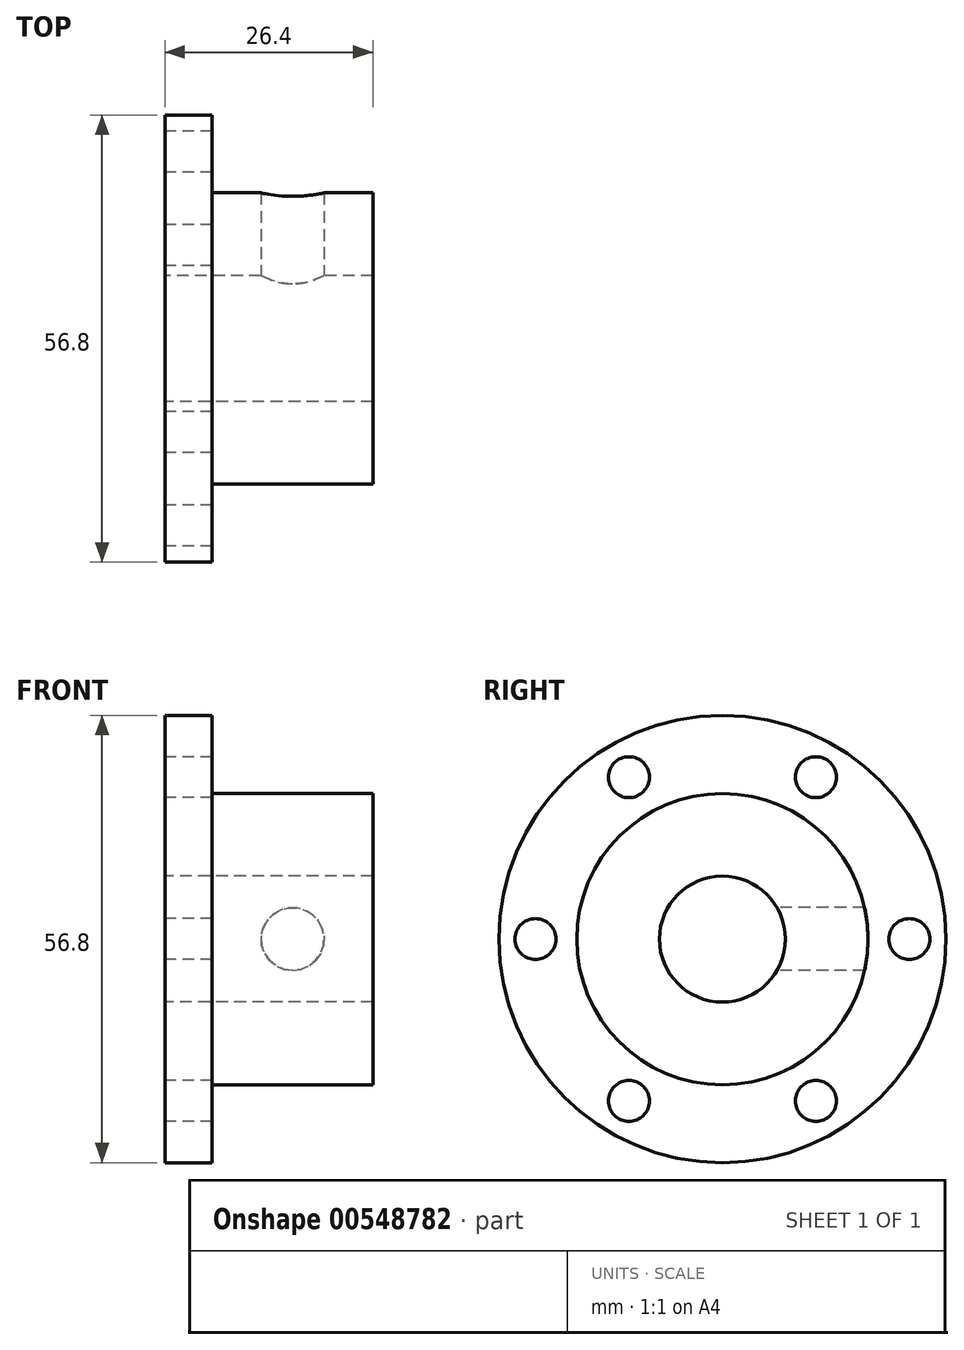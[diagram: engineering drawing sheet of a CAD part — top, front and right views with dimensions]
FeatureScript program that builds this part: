
annotation { "Feature Type Name" : "Feature", "Feature Type Description" : "" }
export const myFeature = defineFeature(function(context is Context, id is Id, definition is map)
    precondition{}
    {
        {
            var Q0;
            Q0=qCreatedBy(makeId("Front.planeOp"),FACE);
            var sketch = newSketch(context, id + "F0", { "sketchPlane" : qUnion([Q0])});
            skLineSegment(sketch, "E0", {"start": v(-18.27, 0) * mm, "end": v(528.92, 0) * mm});
            skLineSegment(sketch, "E1", {"start": v(-18.27, 8) * mm, "end": v(8.13, 8) * mm});
            skLineSegment(sketch, "E2", {"start": v(8.13, 8) * mm, "end": v(8.13, 18.5) * mm});
            skLineSegment(sketch, "E3", {"start": v(8.13, 18.5) * mm, "end": v(-12.27, 18.5) * mm});
            skLineSegment(sketch, "E4", {"start": v(-12.27, 18.5) * mm, "end": v(-12.27, 28.4) * mm});
            skLineSegment(sketch, "E5", {"start": v(-12.27, 28.4) * mm, "end": v(-18.27, 28.4) * mm});
            skLineSegment(sketch, "E6", {"start": v(-18.27, 28.4) * mm, "end": v(-18.27, 8) * mm});
            skSolve(sketch);
        }
        {
            var Q0;
            Q0 = qSketchRegion(id + "F0", true);
            var Q1;
            Q1=sQuery(id+"F0.wireOp",EDGE,"E0");
            revolve(context, id + "F1", {"entities" : qUnion([Q0]), "axis" : qUnion([Q1]), "revolveType" : RevolveType.FULL});
        }
        {
            var Q0;
            Q0=makeQuery(id+"F1.opRevolve","SWEPT_FACE",FACE,{"disambiguationData":[OSD([sQuery(id+"F0.wireOp",EDGE,"E6")])]});
            var sketch = newSketch(context, id + "F2", { "sketchPlane" : qUnion([Q0])});
            skLineSegment(sketch, "E7", {"start": v(0, 0) * mm, "end": v(-22.14, 0) * mm, "construction": true});
            skCircle(sketch, "E8", {"center": v(-23.75, 0) * mm, "radius": 2.6 * mm});
            skCircle(sketch, "E9.1.0", {"center": v(-11.88, -20.57) * mm, "radius": 2.6 * mm});
            skCircle(sketch, "E9.2.0", {"center": v(11.87, -20.57) * mm, "radius": 2.6 * mm});
            skCircle(sketch, "E9.3.0", {"center": v(23.75, 0) * mm, "radius": 2.6 * mm});
            skCircle(sketch, "E9.4.0", {"center": v(11.88, 20.57) * mm, "radius": 2.6 * mm});
            skCircle(sketch, "E9.5.0", {"center": v(-11.88, 20.57) * mm, "radius": 2.6 * mm});
            skPoint(sketch, "E9.center", {"position": v(0, 0) * mm});
            skSolve(sketch);
        }
        {
            var Q0;
            Q0 = qSketchRegion(id + "F2", true);
            extrude(context, id + "F3", {"entities" : qUnion([Q0]), "operationType" : NewBodyOperationType.REMOVE, "endBound" : BoundingType.THROUGH_ALL, "oppositeDirection" : true, "depth" : 25 * mm, "offsetDistance" : 25 * mm});
        }
        {
            var Q0;
            Q0=qCreatedBy(makeId("Front.planeOp"),FACE);
            var sketch = newSketch(context, id + "F4", { "sketchPlane" : qUnion([Q0])});
            skCircle(sketch, "E10", {"center": v(-2.07, 0) * mm, "radius": 4 * mm});
            skSolve(sketch);
        }
        {
            var Q0;
            Q0=makeQuery(id+"F4.imprint","IMPRINT",FACE,{"disambiguationData":[TD([[makeQuery(id+"F4.imprint","IMPRINT",EDGE,{"derivedFrom":sQuery(id+"F4.wireOp",EDGE,"E10")}),1.0]])]});
            var Q1;
            Q1=sQuery(id+"F4.wireOp",EDGE,"E10");
            extrude(context, id + "F5", {"entities" : qUnion([Q0]), "operationType" : NewBodyOperationType.REMOVE, "surfaceEntities" : qUnion([Q1]), "endBound" : BoundingType.THROUGH_ALL, "oppositeDirection" : true, "depth" : 25 * mm, "offsetDistance" : 25 * mm});
        }
    });
